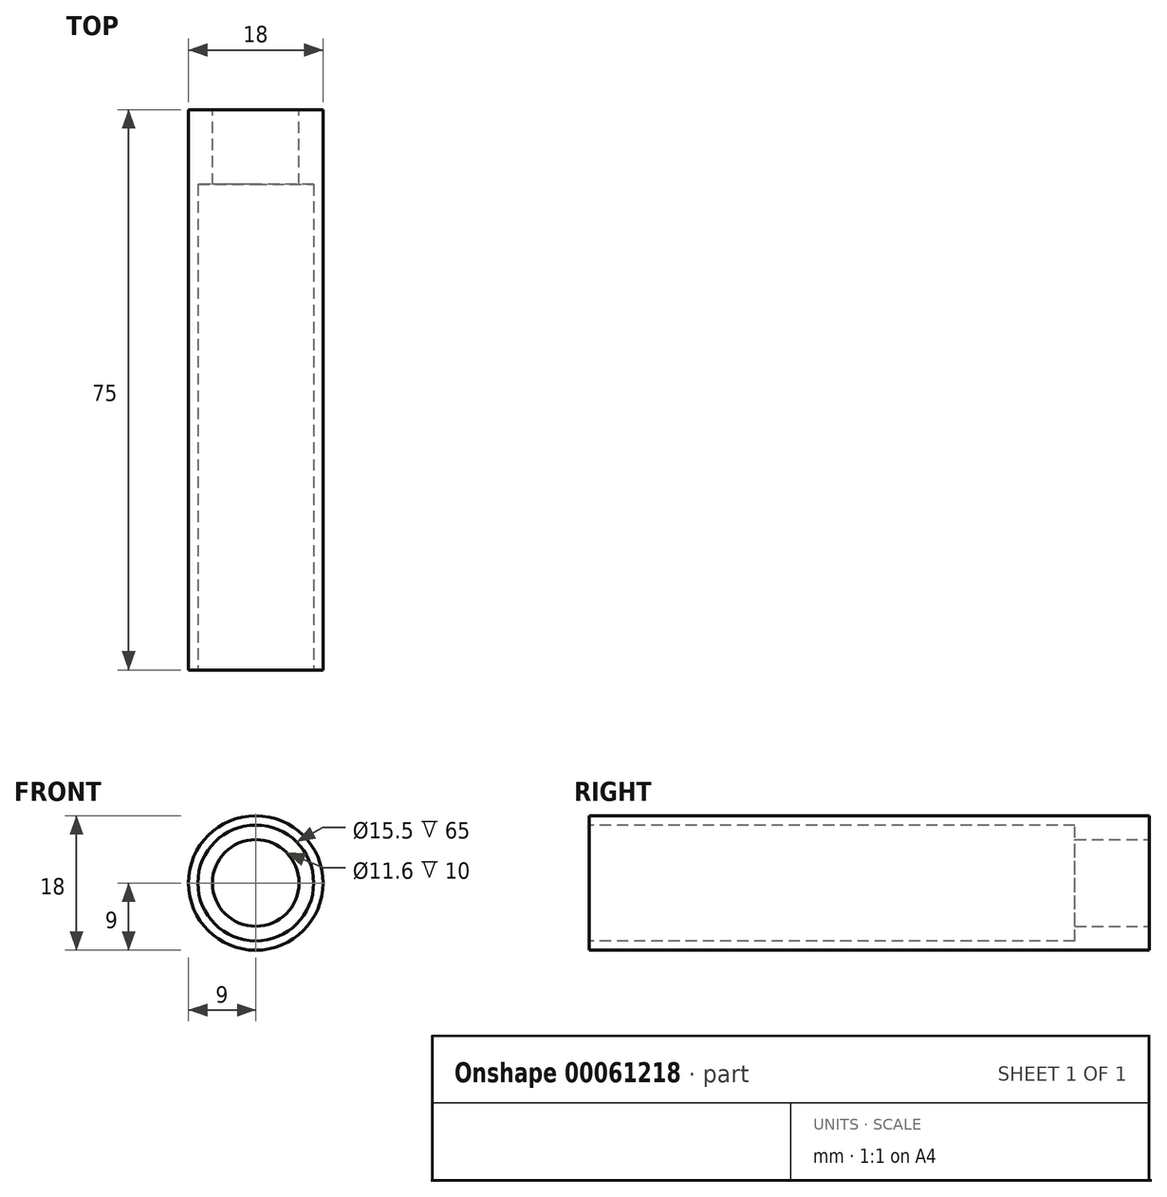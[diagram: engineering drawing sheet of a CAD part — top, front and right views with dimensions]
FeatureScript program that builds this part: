
annotation { "Feature Type Name" : "Feature", "Feature Type Description" : "" }
export const myFeature = defineFeature(function(context is Context, id is Id, definition is map)
    precondition{}
    {
        {
            var Q0;
            Q0=qCreatedBy(makeId("Front.planeOp"),FACE);
            var sketch = newSketch(context, id + "F0", { "sketchPlane" : qUnion([Q0])});
            skCircle(sketch, "E0", {"center": v(0, 0) * mm, "radius": 9 * mm});
            skSolve(sketch);
        }
        {
            var Q0;
            Q0 = qSketchRegion(id + "F0", true);
            extrude(context, id + "F1", {"entities" : qUnion([Q0]), "depth" : 75 * mm});
        }
        {
            var Q0;
            Q0=makeQuery(id+"F1.opExtrude","CAP_FACE",FACE,{"disambiguationData":[OSD([sQuery(id+"F0.wireOp",EDGE,"E0")])],"isStart":false});
            var sketch = newSketch(context, id + "F2", { "sketchPlane" : qUnion([Q0])});
            skCircle(sketch, "E1", {"center": v(0, 0) * mm, "radius": 7.75 * mm});
            skSolve(sketch);
        }
        {
            var Q0;
            Q0 = qSketchRegion(id + "F2", true);
            extrude(context, id + "F3", {"entities" : qUnion([Q0]), "operationType" : NewBodyOperationType.REMOVE, "oppositeDirection" : true, "depth" : 65 * mm});
        }
        {
            var Q0;
            Q0=makeQuery(id+"F1.opExtrude","CAP_FACE",FACE,{"disambiguationData":[OSD([sQuery(id+"F0.wireOp",EDGE,"E0")])],"isStart":true});
            var sketch = newSketch(context, id + "F4", { "sketchPlane" : qUnion([Q0])});
            skCircle(sketch, "E2", {"center": v(0, 0) * mm, "radius": 5.8 * mm});
            skSolve(sketch);
        }
        {
            var Q0;
            Q0 = qSketchRegion(id + "F4", true);
            extrude(context, id + "F5", {"entities" : qUnion([Q0]), "operationType" : NewBodyOperationType.REMOVE, "endBound" : BoundingType.THROUGH_ALL, "oppositeDirection" : true, "depth" : 25 * mm});
        }
    });
